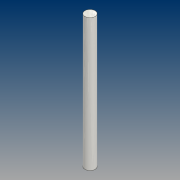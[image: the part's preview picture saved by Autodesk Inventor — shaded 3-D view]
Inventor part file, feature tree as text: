
AUTODESK INVENTOR PART (.ipt)
format: ipt  version: 2021 (Build 250183000, 183)  size: 80,384 bytes
history: native  units: mm
features: extrude x1, sketch x1
ambient origin geometry x8: Origin, YZ Plane, XZ Plane, XY Plane, X Axis, Y Axis, Z Axis, Center Point
bodies: Solid1 (feature_tree)
feature tree (2):
  extrude  "Extrusion1"  Depth=130.0mm TaperAngle=0.0deg
  sketch  "Sketch1"  dims[d0=10.0mm d1=130.0mm d2=0.0mm]
